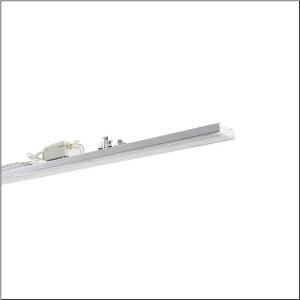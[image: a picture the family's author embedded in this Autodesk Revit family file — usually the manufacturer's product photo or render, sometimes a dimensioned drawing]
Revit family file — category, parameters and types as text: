
# Revit family: licross_11_recessed_mo_51tl12cn44xg
name_source: partatom
category: Lighting Fixtures
units: mm (PartAtom-declared; Revit-internal decimal feet)

## family parameters
Cut with Voids When Loaded = No
Host = Face
Light Source = No
Part Type = Normal
Room Calculation Point = No
Round Connector Dimension = Use Diameter
Shared = No

## types (1)
- Licross 11 Recessed MO (1 x LED, 4300 lm, 21.9 W, 4000K)
    Apparent Load = 22 VA
    CIE Flux Codes = 67 92 99 100 100
    Color Rendering = 80
    Color Temperature = 4000K
    Default Elevation = 1800 mm
    Description = Licross 11 Recessed MO, luminaire insert, of sheet steel, coil coated, white, length: 1.500mm, width: 66mm, height: 67mm, LED rated luminous flux: 4.300lm, light colour: 840, SDCM (Standard Deviation of Colour Matching)MacAdam ≤ 2 SDCM (initial), control gear: ON/OFF, CLOi, with plug, 3-pole, with phase selection, mains connection: 220..240V, AC, 50/60Hz, start of lifetime: 22W, end of service life: 24W, internal wiring halogen-free, primary optical cover: cover, of PMMA, light emission: direct distribution, primary light characteristic: symmetric, protection rating (complete): IP40, insulation class (complete): insulation class I (protective earthing), certification: CE, ENEC, VDE, UKCA, protection symbol: D if used in an environment without relevant dust loads with corresponding accessories, impact resistance: IK06, permissible ambient temperature for indoor applications: -35..+50°C, corresponds to IFS (International Featured Standards) requirements for safety and quality in the food industry, reducing of maximum allowable ambient temperature of 5°C with ceiling mounting, LABS conformity tested according to VDMA 24364:2018-05, The light source and the operating device comply with the requirements of the Ecodesign Regulation (EU) 2019/2020 and are replaceable in accordance with this regulation, packaging unit: 1 piece
    Height = 58 mm
    Lamp = 1 x LED
    Lamp Light Flux = 4300 lm
    Lamp Power = 21.9 W
    Lamp count = 1
    Length = 1500 mm
    Luminous efficacy = 196 lm/W
    Manufacturer = Siteco
    ModVariant = No
    Model = 51TL12CN44XG
    Mounting Place = Ceiling
    Mounting Type = Pendant
    Number of Poles = 1
    OnlyDefault = Yes
    Power Factor = 1
    Product Name = Licross 11 Recessed MO
    Product group = luminaire insert | ceiling pendant
    ProductGroupID = 901
    Protection Class = Protection class I
    Protection Degree = IP 40
    RLX_Detail_Level = 1
    RLX_Emergency_Light_Flux = 0 lm
    RLX_Emergency_Type = 0
    RLX_Emergency_Type_DB = No
    RlxData = <blob elided: 21105 chars, md5=69634052>
    Socket = socket
    Standby Power = 0 W
    System Light Flux = 4300 lm
    System Power = 22 W
    Type Comments = Product without accessories
    Type Image = l_1296930.jpg
    URL = http://relux.com
    VarID = ---
    Voltage = 0 V
    Weight = 0.00 kg
    Width = 66 mm

## geometry (parser evidence)
native form markers: Blend x4, Sweep x10
no freeform markers — native parametric forms only
